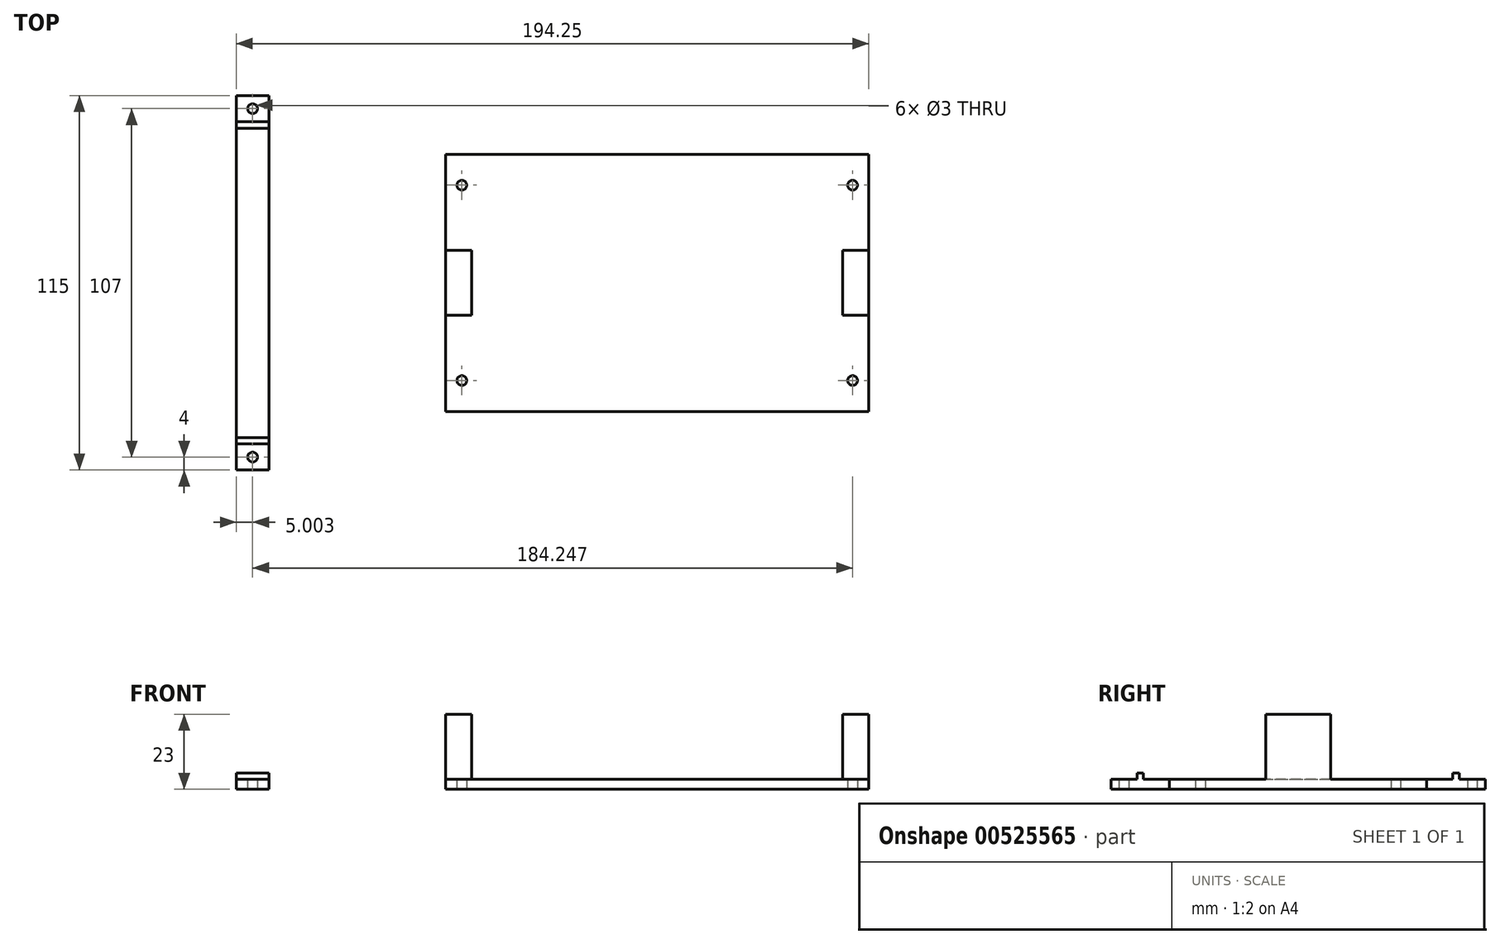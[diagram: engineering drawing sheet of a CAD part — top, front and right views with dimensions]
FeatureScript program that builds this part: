
annotation { "Feature Type Name" : "Feature", "Feature Type Description" : "" }
export const myFeature = defineFeature(function(context is Context, id is Id, definition is map)
    precondition{}
    {
        {
            var Q0;
            Q0=qCreatedBy(makeId("Top.planeOp"),FACE);
            var sketch = newSketch(context, id + "F0", { "sketchPlane" : qUnion([Q0])});
            skLineSegment(sketch, "E0.bottom", {"start": v(55, -39.5) * mm, "end": v(-55, -39.5) * mm});
            skLineSegment(sketch, "E0.top", {"start": v(55, 39.5) * mm, "end": v(-55, 39.5) * mm});
            skLineSegment(sketch, "E0.left", {"start": v(55, -39.5) * mm, "end": v(55, 39.5) * mm});
            skLineSegment(sketch, "E0.right", {"start": v(-55, -39.5) * mm, "end": v(-55, 39.5) * mm});
            skPoint(sketch, "E0.middle", {"position": v(0, 0) * mm});
            skLineSegment(sketch, "E1.bottom", {"start": v(53, -37.5) * mm, "end": v(-53, -37.5) * mm, "construction": true});
            skLineSegment(sketch, "E1.top", {"start": v(53, 37.5) * mm, "end": v(-53, 37.5) * mm, "construction": true});
            skLineSegment(sketch, "E1.left", {"start": v(53, -37.5) * mm, "end": v(53, 37.5) * mm, "construction": true});
            skLineSegment(sketch, "E1.right", {"start": v(-53, -37.5) * mm, "end": v(-53, 37.5) * mm, "construction": true});
            skLineSegment(sketch, "E2.bottom", {"start": v(-55, 39.5) * mm, "end": v(-65, 39.5) * mm});
            skLineSegment(sketch, "E2.top", {"start": v(-55, -39.5) * mm, "end": v(-65, -39.5) * mm});
            skLineSegment(sketch, "E2.left", {"start": v(-55, 39.5) * mm, "end": v(-55, -39.5) * mm});
            skLineSegment(sketch, "E2.right", {"start": v(-65, 39.5) * mm, "end": v(-65, -39.5) * mm});
            skLineSegment(sketch, "E3.bottom", {"start": v(55, 39.5) * mm, "end": v(65, 39.5) * mm});
            skLineSegment(sketch, "E3.top", {"start": v(55, -39.5) * mm, "end": v(65, -39.5) * mm});
            skLineSegment(sketch, "E3.left", {"start": v(55, 39.5) * mm, "end": v(55, -39.5) * mm});
            skLineSegment(sketch, "E3.right", {"start": v(65, 39.5) * mm, "end": v(65, -39.5) * mm});
            skCircle(sketch, "E4", {"center": v(-60, 30) * mm, "radius": 1.5 * mm});
            skPoint(sketch, "E4.centerSnap0", {"position": v(-60, 39.5) * mm});
            skCircle(sketch, "E5", {"center": v(-60, -30) * mm, "radius": 1.5 * mm});
            skCircle(sketch, "E6", {"center": v(60, 30) * mm, "radius": 1.5 * mm});
            skPoint(sketch, "E6.centerSnap0", {"position": v(60, 39.5) * mm});
            skCircle(sketch, "E7", {"center": v(60, -30) * mm, "radius": 1.5 * mm});
            skSolve(sketch);
        }
        {
            var Q0;
            Q0 = qSketchRegion(id + "F0", true);
            extrude(context, id + "F1", {"entities" : qUnion([Q0]), "depth" : 3 * mm, "offsetDistance" : 25 * mm});
        }
        {
            var Q0;
            Q0=makeQuery(id+"F1.opExtrude","CAP_FACE",FACE,{"disambiguationData":[OSD([sQuery(id+"F0.wireOp",EDGE,"E0.bottom"),sQuery(id+"F0.wireOp",EDGE,"E0.top"),sQuery(id+"F0.wireOp",EDGE,"E2.bottom"),sQuery(id+"F0.wireOp",EDGE,"E2.top"),sQuery(id+"F0.wireOp",EDGE,"E2.right"),sQuery(id+"F0.wireOp",EDGE,"E3.bottom"),sQuery(id+"F0.wireOp",EDGE,"E3.top"),sQuery(id+"F0.wireOp",EDGE,"E3.right"),sQuery(id+"F0.wireOp",EDGE,"E4"),sQuery(id+"F0.wireOp",EDGE,"E5"),sQuery(id+"F0.wireOp",EDGE,"E6"),sQuery(id+"F0.wireOp",EDGE,"E7")])],"isStart":false});
            var sketch = newSketch(context, id + "F2", { "sketchPlane" : qUnion([Q0])});
            skLineSegment(sketch, "E8.bottom", {"start": v(-65, 10) * mm, "end": v(-57, 10) * mm});
            skLineSegment(sketch, "E8.top", {"start": v(-65, -10) * mm, "end": v(-57, -10) * mm});
            skLineSegment(sketch, "E8.left", {"start": v(-65, 10) * mm, "end": v(-65, -10) * mm});
            skLineSegment(sketch, "E8.right", {"start": v(-57, 10) * mm, "end": v(-57, -10) * mm});
            skLineSegment(sketch, "E9.MirrorCS", {"start": v(65, 10) * mm, "end": v(65, -10) * mm});
            skLineSegment(sketch, "E10.MirrorCS", {"start": v(57, 10) * mm, "end": v(57, -10) * mm});
            skLineSegment(sketch, "E11.MirrorCS", {"start": v(65, 10) * mm, "end": v(57, 10) * mm});
            skLineSegment(sketch, "E12.MirrorCS", {"start": v(65, -10) * mm, "end": v(57, -10) * mm});
            skSolve(sketch);
        }
        {
            var Q0;
            Q0 = qSketchRegion(id + "F2", true);
            extrude(context, id + "F3", {"entities" : qUnion([Q0]), "operationType" : NewBodyOperationType.ADD, "depth" : 20 * mm, "offsetDistance" : 25 * mm});
        }
        {
            var Q0;
            Q0=qCreatedBy(makeId("Top.planeOp"),FACE);
            var sketch = newSketch(context, id + "F4", { "sketchPlane" : qUnion([Q0])});
            skLineSegment(sketch, "E13.bottom", {"start": v(-119.25, -47.5) * mm, "end": v(-129.25, -47.5) * mm});
            skLineSegment(sketch, "E13.top", {"start": v(-119.25, 47.5) * mm, "end": v(-129.25, 47.5) * mm});
            skLineSegment(sketch, "E13.left", {"start": v(-119.25, -47.5) * mm, "end": v(-119.25, 47.5) * mm});
            skLineSegment(sketch, "E13.right", {"start": v(-129.25, -47.5) * mm, "end": v(-129.25, 47.5) * mm});
            skPoint(sketch, "E13.middle", {"position": v(-124.25, 0) * mm});
            skLineSegment(sketch, "E14.bottom", {"start": v(-129.25, 47.5) * mm, "end": v(-119.25, 47.5) * mm});
            skLineSegment(sketch, "E14.top", {"start": v(-129.25, 57.5) * mm, "end": v(-119.25, 57.5) * mm});
            skLineSegment(sketch, "E14.left", {"start": v(-129.25, 47.5) * mm, "end": v(-129.25, 57.5) * mm});
            skLineSegment(sketch, "E14.right", {"start": v(-119.25, 47.5) * mm, "end": v(-119.25, 57.5) * mm});
            skLineSegment(sketch, "E15.bottom", {"start": v(-129.25, -47.5) * mm, "end": v(-119.25, -47.5) * mm});
            skLineSegment(sketch, "E15.top", {"start": v(-129.25, -57.5) * mm, "end": v(-119.25, -57.5) * mm});
            skLineSegment(sketch, "E15.left", {"start": v(-129.25, -47.5) * mm, "end": v(-129.25, -57.5) * mm});
            skLineSegment(sketch, "E15.right", {"start": v(-119.25, -47.5) * mm, "end": v(-119.25, -57.5) * mm});
            skCircle(sketch, "E16", {"center": v(-124.25, 53.5) * mm, "radius": 1.5 * mm});
            skPoint(sketch, "E16.centerSnap0", {"position": v(-124.25, 57.5) * mm});
            skCircle(sketch, "E17", {"center": v(-124.25, -53.5) * mm, "radius": 1.5 * mm});
            skPoint(sketch, "E17.centerSnap0", {"position": v(-124.25, -57.5) * mm});
            skSolve(sketch);
        }
        {
            var Q0;
            Q0 = qSketchRegion(id + "F4", true);
            extrude(context, id + "F5", {"entities" : qUnion([Q0]), "depth" : 3 * mm, "offsetDistance" : 25 * mm});
        }
        {
            var Q0;
            Q0=makeQuery(id+"F5.opExtrude","CAP_FACE",FACE,{"disambiguationData":[OSD([sQuery(id+"F4.wireOp",EDGE,"E13.left"),sQuery(id+"F4.wireOp",EDGE,"E13.right"),sQuery(id+"F4.wireOp",EDGE,"E14.top"),sQuery(id+"F4.wireOp",EDGE,"E14.left"),sQuery(id+"F4.wireOp",EDGE,"E14.right"),sQuery(id+"F4.wireOp",EDGE,"E15.top"),sQuery(id+"F4.wireOp",EDGE,"E15.left"),sQuery(id+"F4.wireOp",EDGE,"E15.right")])],"isStart":false});
            var sketch = newSketch(context, id + "F6", { "sketchPlane" : qUnion([Q0])});
            skLineSegment(sketch, "E18.bottom", {"start": v(-129.25, 49.5) * mm, "end": v(-119.25, 49.5) * mm});
            skLineSegment(sketch, "E18.top", {"start": v(-129.25, 47.5) * mm, "end": v(-119.25, 47.5) * mm});
            skLineSegment(sketch, "E18.left", {"start": v(-129.25, 49.5) * mm, "end": v(-129.25, 47.5) * mm});
            skLineSegment(sketch, "E18.right", {"start": v(-119.25, 49.5) * mm, "end": v(-119.25, 47.5) * mm});
            skLineSegment(sketch, "E19.bottom", {"start": v(-129.25, -49.5) * mm, "end": v(-119.25, -49.5) * mm});
            skLineSegment(sketch, "E19.top", {"start": v(-129.25, -47.5) * mm, "end": v(-119.25, -47.5) * mm});
            skLineSegment(sketch, "E19.left", {"start": v(-129.25, -49.5) * mm, "end": v(-129.25, -47.5) * mm});
            skLineSegment(sketch, "E19.right", {"start": v(-119.25, -49.5) * mm, "end": v(-119.25, -47.5) * mm});
            skSolve(sketch);
        }
        {
            var Q0;
            Q0 = qSketchRegion(id + "F6", true);
            extrude(context, id + "F7", {"entities" : qUnion([Q0]), "operationType" : NewBodyOperationType.ADD, "depth" : 2 * mm, "offsetDistance" : 25 * mm});
        }
    });
